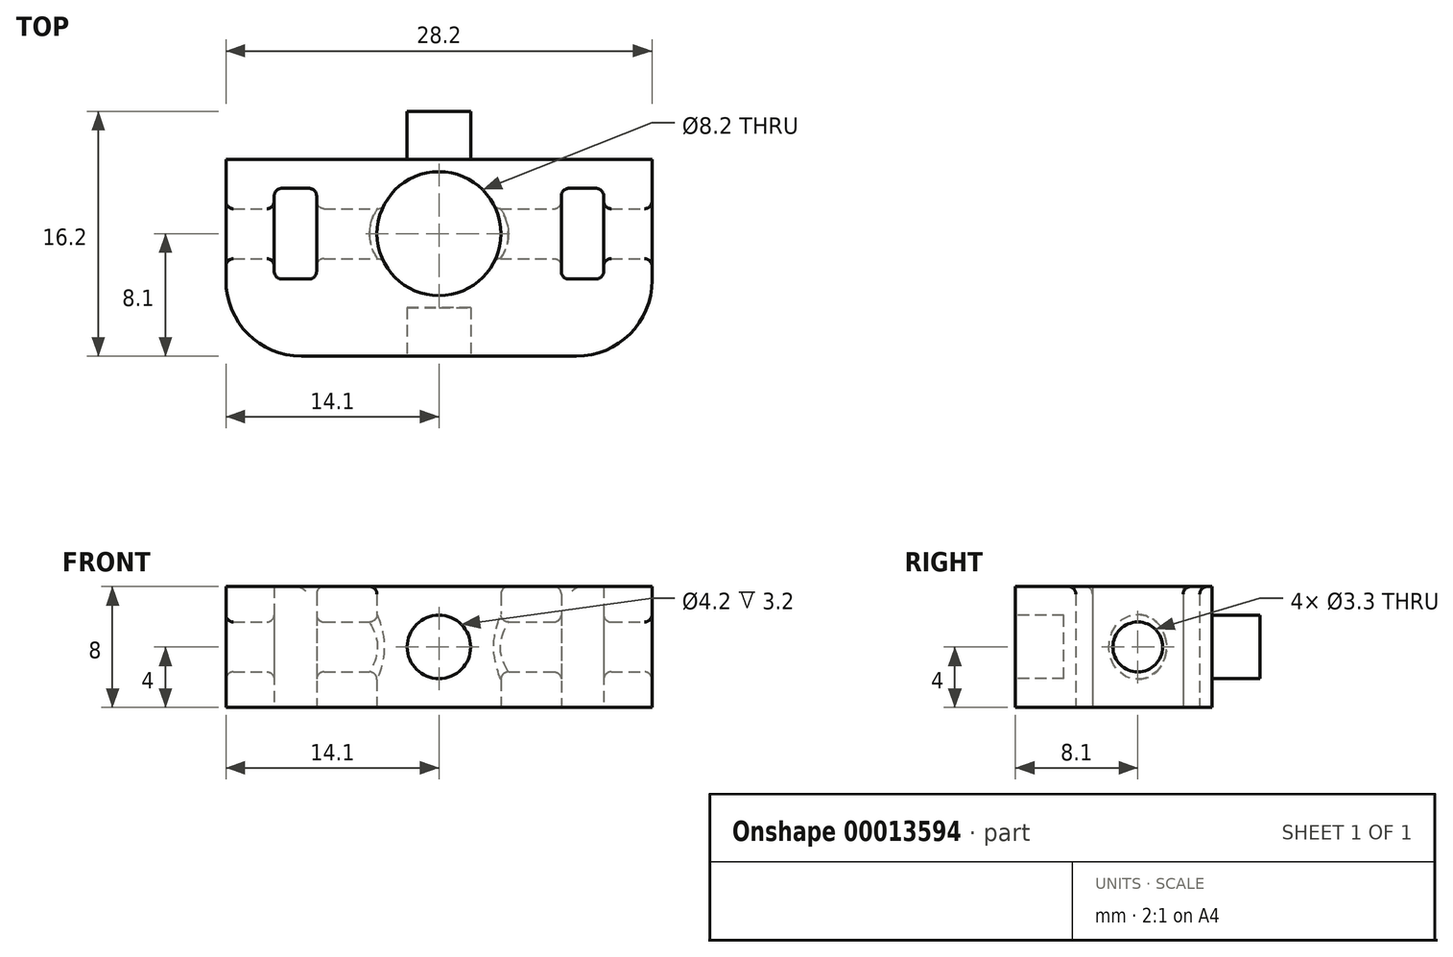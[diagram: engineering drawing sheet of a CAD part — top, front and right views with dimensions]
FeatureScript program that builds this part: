
annotation { "Feature Type Name" : "Feature", "Feature Type Description" : "" }
export const myFeature = defineFeature(function(context is Context, id is Id, definition is map)
    precondition{}
    {
        {
            var Q0;
            Q0=qCreatedBy(makeId("Top.planeOp"),FACE);
            var sketch = newSketch(context, id + "F0", { "sketchPlane" : qUnion([Q0])});
            skCircle(sketch, "E0", {"center": v(0, 0) * mm, "radius": 4.1 * mm});
            skLineSegment(sketch, "E1.rect.bottom", {"start": v(-8.1, -3) * mm, "end": v(-10.9, -3) * mm});
            skLineSegment(sketch, "E1.rect.top", {"start": v(-8.1, 3) * mm, "end": v(-10.9, 3) * mm});
            skLineSegment(sketch, "E1.rect.left", {"start": v(-8.1, -3) * mm, "end": v(-8.1, 3) * mm});
            skLineSegment(sketch, "E1.rect.right", {"start": v(-10.9, -3) * mm, "end": v(-10.9, 3) * mm});
            skPoint(sketch, "E1.rect.middle", {"position": v(-9.5, 0) * mm});
            skLineSegment(sketch, "E2", {"start": v(0, 0) * mm, "end": v(0, 4.1) * mm, "construction": true});
            skLineSegment(sketch, "E3.rect.bottom", {"start": v(-14.1, 8.1) * mm, "end": v(14.1, 8.1) * mm});
            skLineSegment(sketch, "E3.rect.top", {"start": v(-14.1, -8.1) * mm, "end": v(14.1, -8.1) * mm});
            skLineSegment(sketch, "E3.rect.left", {"start": v(-14.1, 8.1) * mm, "end": v(-14.1, -8.1) * mm});
            skLineSegment(sketch, "E3.rect.right", {"start": v(14.1, 8.1) * mm, "end": v(14.1, -8.1) * mm});
            skLineSegment(sketch, "E4.rect.bottom", {"start": v(2.1, 8.1) * mm, "end": v(-2.1, 8.1) * mm, "construction": true});
            skLineSegment(sketch, "E4.rect.top", {"start": v(2.1, 4.9) * mm, "end": v(-2.1, 4.9) * mm, "construction": true});
            skLineSegment(sketch, "E4.rect.left", {"start": v(2.1, 8.1) * mm, "end": v(2.1, 4.9) * mm, "construction": true});
            skLineSegment(sketch, "E4.rect.right", {"start": v(-2.1, 8.1) * mm, "end": v(-2.1, 4.9) * mm, "construction": true});
            skPoint(sketch, "E4.rect.middle", {"position": v(0, 6.5) * mm});
            skLineSegment(sketch, "E5.0.MirrorCS", {"start": v(8.1, -3) * mm, "end": v(8.1, 3) * mm});
            skLineSegment(sketch, "E6.0.MirrorCS", {"start": v(8.1, 3) * mm, "end": v(10.9, 3) * mm});
            skLineSegment(sketch, "E7.0.MirrorCS", {"start": v(10.9, -3) * mm, "end": v(10.9, 3) * mm});
            skLineSegment(sketch, "E8.0.MirrorCS", {"start": v(8.1, -3) * mm, "end": v(10.9, -3) * mm});
            skLineSegment(sketch, "E9", {"start": v(0, 0) * mm, "end": v(4.1, 0) * mm, "construction": true});
            skLineSegment(sketch, "E10.0.MirrorCS", {"start": v(2.1, -4.9) * mm, "end": v(-2.1, -4.9) * mm, "construction": true});
            skLineSegment(sketch, "E11.0.MirrorCS", {"start": v(2.1, -8.1) * mm, "end": v(2.1, -4.9) * mm, "construction": true});
            skLineSegment(sketch, "E12.0.MirrorCS", {"start": v(2.1, -8.1) * mm, "end": v(-2.1, -8.1) * mm, "construction": true});
            skLineSegment(sketch, "E13.0.MirrorCS", {"start": v(-2.1, -8.1) * mm, "end": v(-2.1, -4.9) * mm, "construction": true});
            skSolve(sketch);
        }
        {
            var Q0;
            Q0=makeQuery(id+"F0.imprint","IMPRINT",FACE,{"disambiguationData":[TD([[makeQuery(id+"F0.imprint","IMPRINT",EDGE,{"derivedFrom":sQuery(id+"F0.wireOp",EDGE,"E0")}),-1.0]])]});
            extrude(context, id + "F1", {"entities" : qUnion([Q0]), "depth" : 8 * mm});
        }
        {
            var Q0;
            Q0=makeQuery(id+"F1.opExtrude","SWEPT_FACE",FACE,{"disambiguationData":[OSD([sQuery(id+"F0.wireOp",EDGE,"E3.rect.right")])]});
            var sketch = newSketch(context, id + "F2", { "sketchPlane" : qUnion([Q0])});
            skCircle(sketch, "E14", {"center": v(0, 4) * mm, "radius": 1.65 * mm});
            skLineSegment(sketch, "E15", {"start": v(0, 4) * mm, "end": v(8.1, 4) * mm, "construction": true});
            skSolve(sketch);
        }
        {
            var Q0;
            Q0=qSketchRegion(id+"F2",true);
            var Q1;
            Q1=makeQuery(id+"F2.imprint","IMPRINT",FACE,{"disambiguationData":[TD([[makeQuery(id+"F2.imprint","IMPRINT",EDGE,{"derivedFrom":sQuery(id+"F2.wireOp",EDGE,"E14")}),1.0]])]});
            extrude(context, id + "F3", {"entities" : qUnion([Q0, Q1]), "operationType" : NewBodyOperationType.REMOVE, "endBound" : BoundingType.THROUGH_ALL, "oppositeDirection" : true, "depth" : 25 * mm});
        }
        {
            var Q0;
            Q0=makeQuery(id+"F1.opExtrude","SWEPT_FACE",FACE,{"disambiguationData":[OSD([sQuery(id+"F0.wireOp",EDGE,"E3.rect.top")])]});
            var sketch = newSketch(context, id + "F4", { "sketchPlane" : qUnion([Q0])});
            skLineSegment(sketch, "E16", {"start": v(0, 0) * mm, "end": v(0, 8) * mm, "construction": true});
            skCircle(sketch, "E17", {"center": v(0, 4) * mm, "radius": 2.1 * mm});
            skPoint(sketch, "E18.0", {"position": v(2.1, 0) * mm});
            skLineSegment(sketch, "E19", {"start": v(2.1, 0) * mm, "end": v(2.1, 8) * mm, "construction": true});
            skSolve(sketch);
        }
        {
            var Q0;
            Q0=makeQuery(id+"F1.opExtrude","SWEPT_FACE",FACE,{"disambiguationData":[OSD([sQuery(id+"F0.wireOp",EDGE,"E3.rect.bottom")])]});
            var sketch = newSketch(context, id + "F5", { "sketchPlane" : qUnion([Q0])});
            skPoint(sketch, "E20.0", {"position": v(2.1, 0) * mm});
            skCircle(sketch, "E21.0", {"center": v(0, 4) * mm, "radius": 2.1 * mm});
            skSolve(sketch);
        }
        {
            var Q0;
            Q0=makeQuery(id+"F4.imprint","IMPRINT",FACE,{"disambiguationData":[TD([[makeQuery(id+"F4.imprint","IMPRINT",EDGE,{"derivedFrom":sQuery(id+"F4.wireOp",EDGE,"E17")}),1.0]])]});
            extrude(context, id + "F6", {"entities" : qUnion([Q0]), "operationType" : NewBodyOperationType.REMOVE, "oppositeDirection" : true, "depth" : 3.2 * mm});
        }
        {
            var Q0;
            Q0=makeQuery(id+"F5.imprint","IMPRINT",FACE,{"disambiguationData":[TD([[makeQuery(id+"F5.imprint","IMPRINT",EDGE,{"derivedFrom":sQuery(id+"F5.wireOp",EDGE,"E21.0")}),-1.0]])]});
            extrude(context, id + "F7", {"entities" : qUnion([Q0]), "operationType" : NewBodyOperationType.REMOVE, "oppositeDirection" : true, "depth" : 3.2 * mm});
        }
        {
            var Q0;
            Q0=makeQuery(id+"F7.boolean.opBoolean","COPY",EDGE,{"derivedFrom":makeQuery(id+"F7.opExtrude","CAP_EDGE",EDGE,{"disambiguationData":[OSD([sQuery(id+"F5.wireOp",EDGE,"E21.0")])],"isStart":true})});
            var Q1;
            Q1=makeQuery(id+"F6.boolean.opBoolean","COPY",EDGE,{"derivedFrom":makeQuery(id+"F6.opExtrude","CAP_EDGE",EDGE,{"disambiguationData":[OSD([sQuery(id+"F4.wireOp",EDGE,"E17")])],"isStart":true})});
            var Q2;
            Q2=makeQuery(id+"F3.boolean.opBoolean","COPY",FACE,{"disambiguationData":[OD(0.0)],"derivedFrom":makeQuery(id+"F3.opExtrude","SWEPT_FACE",FACE,{"disambiguationData":[OSD([sQuery(id+"F2.wireOp",EDGE,"E14")])]})});
            var Q3;
            Q3=makeQuery(id+"F3.boolean.opBoolean","COPY",FACE,{"disambiguationData":[OD(2.0)],"derivedFrom":makeQuery(id+"F3.opExtrude","SWEPT_FACE",FACE,{"disambiguationData":[OSD([sQuery(id+"F2.wireOp",EDGE,"E14")])]})});
            var Q4;
            Q4=makeQuery(id+"F3.boolean.opBoolean","COPY",FACE,{"disambiguationData":[OD(1.0)],"derivedFrom":makeQuery(id+"F3.opExtrude","SWEPT_FACE",FACE,{"disambiguationData":[OSD([sQuery(id+"F2.wireOp",EDGE,"E14")])]})});
            var Q5;
            Q5=makeQuery(id+"F3.boolean.opBoolean","COPY",FACE,{"disambiguationData":[OD(3.0)],"derivedFrom":makeQuery(id+"F3.opExtrude","SWEPT_FACE",FACE,{"disambiguationData":[OSD([sQuery(id+"F2.wireOp",EDGE,"E14")])]})});
            var Q6;
            Q6=makeQuery(id+"F1.opExtrude","SWEPT_EDGE",EDGE,{"disambiguationData":[OSD([sQuery(id+"F0.wireOp",EDGE,"E5.0.MirrorCS"),sQuery(id+"F0.wireOp",EDGE,"E8.0.MirrorCS")])]});
            var Q7;
            Q7=makeQuery(id+"F1.opExtrude","SWEPT_EDGE",EDGE,{"disambiguationData":[OSD([sQuery(id+"F0.wireOp",EDGE,"E7.0.MirrorCS"),sQuery(id+"F0.wireOp",EDGE,"E8.0.MirrorCS")])]});
            var Q8;
            Q8=makeQuery(id+"F1.opExtrude","SWEPT_EDGE",EDGE,{"disambiguationData":[OSD([sQuery(id+"F0.wireOp",EDGE,"E6.0.MirrorCS"),sQuery(id+"F0.wireOp",EDGE,"E7.0.MirrorCS")])]});
            var Q9;
            Q9=makeQuery(id+"F1.opExtrude","SWEPT_EDGE",EDGE,{"disambiguationData":[OSD([sQuery(id+"F0.wireOp",EDGE,"E5.0.MirrorCS"),sQuery(id+"F0.wireOp",EDGE,"E6.0.MirrorCS")])]});
            var Q10;
            Q10=makeQuery(id+"F1.opExtrude","SWEPT_EDGE",EDGE,{"disambiguationData":[OSD([sQuery(id+"F0.wireOp",EDGE,"E1.rect.top"),sQuery(id+"F0.wireOp",EDGE,"E1.rect.right")])]});
            var Q11;
            Q11=makeQuery(id+"F1.opExtrude","SWEPT_EDGE",EDGE,{"disambiguationData":[OSD([sQuery(id+"F0.wireOp",EDGE,"E1.rect.top"),sQuery(id+"F0.wireOp",EDGE,"E1.rect.left")])]});
            var Q12;
            Q12=makeQuery(id+"F1.opExtrude","SWEPT_EDGE",EDGE,{"disambiguationData":[OSD([sQuery(id+"F0.wireOp",EDGE,"E1.rect.bottom"),sQuery(id+"F0.wireOp",EDGE,"E1.rect.left")])]});
            var Q13;
            Q13=makeQuery(id+"F1.opExtrude","SWEPT_EDGE",EDGE,{"disambiguationData":[OSD([sQuery(id+"F0.wireOp",EDGE,"E1.rect.bottom"),sQuery(id+"F0.wireOp",EDGE,"E1.rect.right")])]});
            var Q14;
            Q14=makeQuery(id+"F1.opExtrude","CAP_EDGE",EDGE,{"disambiguationData":[OSD([sQuery(id+"F0.wireOp",EDGE,"E1.rect.left")])],"isStart":false});
            var Q15;
            Q15=makeQuery(id+"F1.opExtrude","CAP_EDGE",EDGE,{"disambiguationData":[OSD([sQuery(id+"F0.wireOp",EDGE,"E0")])],"isStart":false});
            var Q16;
            Q16=makeQuery(id+"F1.opExtrude","CAP_EDGE",EDGE,{"disambiguationData":[OSD([sQuery(id+"F0.wireOp",EDGE,"E5.0.MirrorCS")])],"isStart":false});
            fillet(context, id + "F8", {"entities" : qUnion([Q0, Q1, Q2, Q3, Q4, Q5, Q6, Q7, Q8, Q9, Q10, Q11, Q12, Q13, Q14, Q15, Q16]), "radius" : 0.5 * mm, "tangentPropagation" : true, "allowEdgeOverflow" : false});
        }
        {
            var Q0;
            Q0=makeQuery(id+"F1.opExtrude","SWEPT_EDGE",EDGE,{"disambiguationData":[OSD([sQuery(id+"F0.wireOp",EDGE,"E3.rect.bottom"),sQuery(id+"F0.wireOp",EDGE,"E3.rect.left")])]});
            var Q1;
            Q1=makeQuery(id+"F1.opExtrude","SWEPT_EDGE",EDGE,{"disambiguationData":[OSD([sQuery(id+"F0.wireOp",EDGE,"E3.rect.top"),sQuery(id+"F0.wireOp",EDGE,"E3.rect.left")])]});
            var Q2;
            Q2=makeQuery(id+"F1.opExtrude","SWEPT_EDGE",EDGE,{"disambiguationData":[OSD([sQuery(id+"F0.wireOp",EDGE,"E3.rect.bottom"),sQuery(id+"F0.wireOp",EDGE,"E3.rect.right")])]});
            var Q3;
            Q3=makeQuery(id+"F1.opExtrude","SWEPT_EDGE",EDGE,{"disambiguationData":[OSD([sQuery(id+"F0.wireOp",EDGE,"E3.rect.top"),sQuery(id+"F0.wireOp",EDGE,"E3.rect.right")])]});
            fillet(context, id + "F9", {"entities" : qUnion([Q0, Q1, Q2, Q3]), "radius" : 5 * mm, "tangentPropagation" : true, "allowEdgeOverflow" : false});
        }
    });
